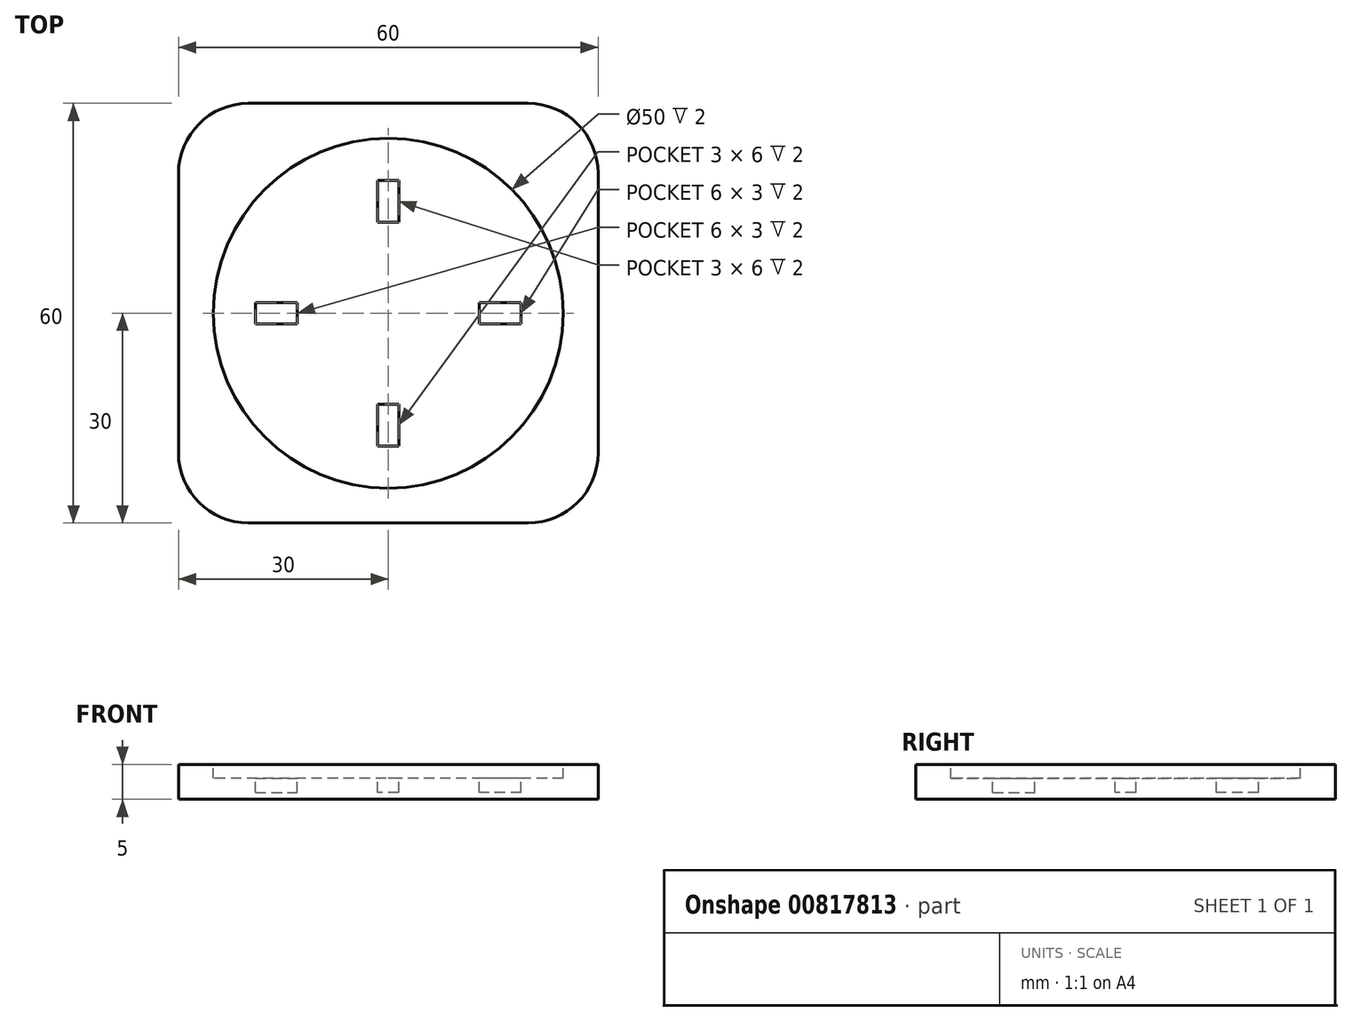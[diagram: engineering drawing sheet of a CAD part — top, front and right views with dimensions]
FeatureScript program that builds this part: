
annotation { "Feature Type Name" : "Feature", "Feature Type Description" : "" }
export const myFeature = defineFeature(function(context is Context, id is Id, definition is map)
    precondition{}
    {
        {
            var Q0;
            Q0=qCreatedBy(makeId("Top.planeOp"),FACE);
            var sketch = newSketch(context, id + "F0", { "sketchPlane" : qUnion([Q0])});
            skLineSegment(sketch, "E0.bottom", {"start": v(30, 30) * mm, "end": v(-30, 30) * mm});
            skLineSegment(sketch, "E0.top", {"start": v(30, -30) * mm, "end": v(-30, -30) * mm});
            skLineSegment(sketch, "E0.left", {"start": v(30, 30) * mm, "end": v(30, -30) * mm});
            skLineSegment(sketch, "E0.right", {"start": v(-30, 30) * mm, "end": v(-30, -30) * mm});
            skPoint(sketch, "E0.middle", {"position": v(0, 0) * mm});
            skSolve(sketch);
        }
        {
            var Q0;
            Q0=makeQuery(id+"F0.imprint","IMPRINT",FACE,{"disambiguationData":[TD([[makeQuery(id+"F0.imprint","IMPRINT",EDGE,{"derivedFrom":sQuery(id+"F0.wireOp",EDGE,"E0.bottom")}),1.0]])]});
            extrude(context, id + "F1", {"entities" : qUnion([Q0]), "depth" : 5 * mm, "offsetDistance" : 25 * mm});
        }
        {
            var Q0;
            Q0=makeQuery(id+"F1.opExtrude","CAP_FACE",FACE,{"disambiguationData":[OSD([sQuery(id+"F0.wireOp",EDGE,"E0.bottom"),sQuery(id+"F0.wireOp",EDGE,"E0.top"),sQuery(id+"F0.wireOp",EDGE,"E0.left"),sQuery(id+"F0.wireOp",EDGE,"E0.right")])],"isStart":false});
            var sketch = newSketch(context, id + "F2", { "sketchPlane" : qUnion([Q0])});
            skCircle(sketch, "E1", {"center": v(0, 0) * mm, "radius": 25 * mm});
            skSolve(sketch);
        }
        {
            var Q0;
            Q0=makeQuery(id+"F2.imprint","IMPRINT",FACE,{"disambiguationData":[TD([[makeQuery(id+"F2.imprint","IMPRINT",EDGE,{"derivedFrom":sQuery(id+"F2.wireOp",EDGE,"E1")}),1.0]])]});
            extrude(context, id + "F3", {"entities" : qUnion([Q0]), "operationType" : NewBodyOperationType.REMOVE, "oppositeDirection" : true, "depth" : 2 * mm, "offsetDistance" : 25 * mm});
        }
        {
            var Q0;
            Q0=makeQuery(id+"F3.boolean.opBoolean","COPY",FACE,{"derivedFrom":makeQuery(id+"F3.opExtrude","CAP_FACE",FACE,{"disambiguationData":[OSD([sQuery(id+"F2.wireOp",EDGE,"E1")])],"isStart":false})});
            var sketch = newSketch(context, id + "F4", { "sketchPlane" : qUnion([Q0])});
            skLineSegment(sketch, "E2.bottom", {"start": v(-1.5, 19) * mm, "end": v(1.5, 19) * mm});
            skLineSegment(sketch, "E2.top", {"start": v(-1.5, 13) * mm, "end": v(1.5, 13) * mm});
            skLineSegment(sketch, "E2.left", {"start": v(-1.5, 19) * mm, "end": v(-1.5, 13) * mm});
            skLineSegment(sketch, "E2.right", {"start": v(1.5, 19) * mm, "end": v(1.5, 13) * mm});
            skPoint(sketch, "E2.middle", {"position": v(0, 16) * mm});
            skLineSegment(sketch, "E3.1.0", {"start": v(-19, 1.5) * mm, "end": v(-13, 1.5) * mm});
            skLineSegment(sketch, "E3.1.1", {"start": v(-19, -1.5) * mm, "end": v(-13, -1.5) * mm});
            skLineSegment(sketch, "E3.1.2", {"start": v(-13, -1.5) * mm, "end": v(-13, 1.5) * mm});
            skLineSegment(sketch, "E3.1.3", {"start": v(-19, -1.5) * mm, "end": v(-19, 1.5) * mm});
            skLineSegment(sketch, "E3.2.0", {"start": v(-1.5, -19) * mm, "end": v(-1.5, -13) * mm});
            skLineSegment(sketch, "E3.2.1", {"start": v(1.5, -19) * mm, "end": v(1.5, -13) * mm});
            skLineSegment(sketch, "E3.2.2", {"start": v(1.5, -13) * mm, "end": v(-1.5, -13) * mm});
            skLineSegment(sketch, "E3.2.3", {"start": v(1.5, -19) * mm, "end": v(-1.5, -19) * mm});
            skLineSegment(sketch, "E3.3.0", {"start": v(19, -1.5) * mm, "end": v(13, -1.5) * mm});
            skLineSegment(sketch, "E3.3.1", {"start": v(19, 1.5) * mm, "end": v(13, 1.5) * mm});
            skLineSegment(sketch, "E3.3.2", {"start": v(13, 1.5) * mm, "end": v(13, -1.5) * mm});
            skLineSegment(sketch, "E3.3.3", {"start": v(19, 1.5) * mm, "end": v(19, -1.5) * mm});
            skPoint(sketch, "E3.center", {"position": v(0, 0) * mm});
            skSolve(sketch);
        }
        {
            var Q0;
            Q0=makeQuery(id+"F4.imprint","IMPRINT",FACE,{"disambiguationData":[TD([[makeQuery(id+"F4.imprint","IMPRINT",EDGE,{"derivedFrom":sQuery(id+"F4.wireOp",EDGE,"E2.bottom")}),-1.0]])]});
            var Q1;
            Q1=makeQuery(id+"F4.imprint","IMPRINT",FACE,{"disambiguationData":[TD([[makeQuery(id+"F4.imprint","IMPRINT",EDGE,{"derivedFrom":sQuery(id+"F4.wireOp",EDGE,"E3.1.0")}),-1.0]])]});
            var Q2;
            Q2=makeQuery(id+"F4.imprint","IMPRINT",FACE,{"disambiguationData":[TD([[makeQuery(id+"F4.imprint","IMPRINT",EDGE,{"derivedFrom":sQuery(id+"F4.wireOp",EDGE,"E3.3.0")}),-1.0]])]});
            var Q3;
            Q3=makeQuery(id+"F4.imprint","IMPRINT",FACE,{"disambiguationData":[TD([[makeQuery(id+"F4.imprint","IMPRINT",EDGE,{"derivedFrom":sQuery(id+"F4.wireOp",EDGE,"E3.2.0")}),-1.0]])]});
            extrude(context, id + "F5", {"entities" : qUnion([Q0, Q1, Q2, Q3]), "operationType" : NewBodyOperationType.REMOVE, "oppositeDirection" : true, "depth" : 2 * mm, "offsetDistance" : 25 * mm});
        }
        {
            var Q0;
            Q0=makeQuery(id+"F1.opExtrude","SWEPT_EDGE",EDGE,{"disambiguationData":[OSD([sQuery(id+"F0.wireOp",EDGE,"E0.top"),sQuery(id+"F0.wireOp",EDGE,"E0.left")])]});
            var Q1;
            Q1=makeQuery(id+"F1.opExtrude","SWEPT_EDGE",EDGE,{"disambiguationData":[OSD([sQuery(id+"F0.wireOp",EDGE,"E0.bottom"),sQuery(id+"F0.wireOp",EDGE,"E0.left")])]});
            var Q2;
            Q2=makeQuery(id+"F1.opExtrude","SWEPT_EDGE",EDGE,{"disambiguationData":[OSD([sQuery(id+"F0.wireOp",EDGE,"E0.bottom"),sQuery(id+"F0.wireOp",EDGE,"E0.right")])]});
            var Q3;
            Q3=makeQuery(id+"F1.opExtrude","SWEPT_EDGE",EDGE,{"disambiguationData":[OSD([sQuery(id+"F0.wireOp",EDGE,"E0.top"),sQuery(id+"F0.wireOp",EDGE,"E0.right")])]});
            fillet(context, id + "F6", {"entities" : qUnion([Q0, Q1, Q2, Q3]), "radius" : 10 * mm, "tangentPropagation" : true, "allowEdgeOverflow" : false});
        }
    });
